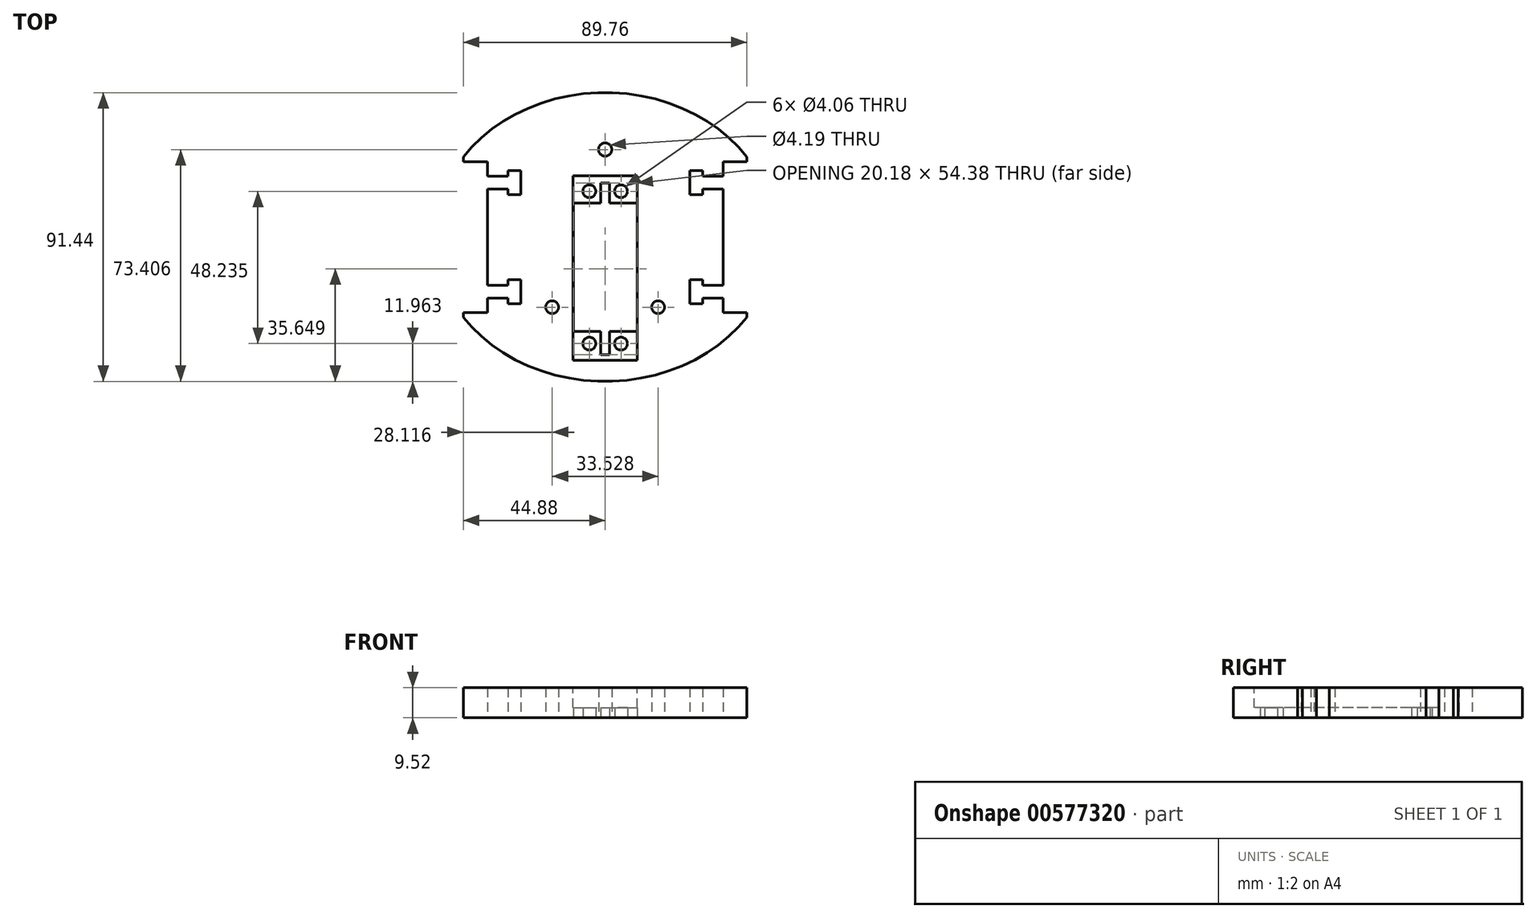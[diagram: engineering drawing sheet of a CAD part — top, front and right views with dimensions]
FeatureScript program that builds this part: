
annotation { "Feature Type Name" : "Feature", "Feature Type Description" : "" }
export const myFeature = defineFeature(function(context is Context, id is Id, definition is map)
    precondition{}
    {
        {
            var Q0;
            Q0=qCreatedBy(makeId("Top.planeOp"),FACE);
            var sketch = newSketch(context, id + "F0", { "sketchPlane" : qUnion([Q0])});
            skEllipticalArc(sketch, "E0", {});
            skLineSegment(sketch, "E1", {"start": v(44.88, 25.4) * mm, "end": v(44.88, 23.81) * mm});
            skLineSegment(sketch, "E2", {"start": v(0, 45.72) * mm, "end": v(0, 29.78) * mm});
            skArc(sketch, "E3", {"start": v(0, 25.6) * mm, "mid": v(2.1, 27.69) * mm, "end": v(0, 29.78) * mm});
            skCircle(sketch, "E4", {"center": v(5, 14.48) * mm, "radius": 2.03 * mm});
            skCircle(sketch, "E5", {"center": v(5, -33.76) * mm, "radius": 2.03 * mm});
            skLineSegment(sketch, "E6", {"start": v(44.88, 23.81) * mm, "end": v(37.26, 23.81) * mm});
            skLineSegment(sketch, "E7", {"start": v(37.26, 23.81) * mm, "end": v(37.26, 19.3) * mm});
            skLineSegment(sketch, "E8", {"start": v(37.26, 19.3) * mm, "end": v(30.78, 19.3) * mm});
            skLineSegment(sketch, "E9", {"start": v(30.78, 19.3) * mm, "end": v(30.78, 21.07) * mm});
            skLineSegment(sketch, "E10", {"start": v(30.78, 21.07) * mm, "end": v(26.72, 21.07) * mm});
            skLineSegment(sketch, "E11", {"start": v(26.72, 21.07) * mm, "end": v(26.72, 13.45) * mm});
            skLineSegment(sketch, "E12", {"start": v(26.72, 13.45) * mm, "end": v(30.78, 13.45) * mm});
            skLineSegment(sketch, "E13", {"start": v(30.78, 13.45) * mm, "end": v(30.78, 15.23) * mm});
            skLineSegment(sketch, "E14", {"start": v(30.78, 15.23) * mm, "end": v(37.26, 15.23) * mm});
            skLineSegment(sketch, "E15", {"start": v(37.26, 15.23) * mm, "end": v(37.26, -15.35) * mm});
            skLineSegment(sketch, "E16", {"start": v(37.26, -15.35) * mm, "end": v(30.78, -15.35) * mm});
            skLineSegment(sketch, "E17", {"start": v(30.78, -15.35) * mm, "end": v(30.78, -13.58) * mm});
            skLineSegment(sketch, "E18", {"start": v(30.78, -13.58) * mm, "end": v(26.72, -13.58) * mm});
            skLineSegment(sketch, "E19", {"start": v(26.72, -13.58) * mm, "end": v(26.72, -21.2) * mm});
            skLineSegment(sketch, "E20", {"start": v(26.72, -21.2) * mm, "end": v(30.78, -21.2) * mm});
            skLineSegment(sketch, "E21", {"start": v(30.78, -21.2) * mm, "end": v(30.78, -19.42) * mm});
            skLineSegment(sketch, "E22", {"start": v(30.78, -19.42) * mm, "end": v(37.26, -19.42) * mm});
            skLineSegment(sketch, "E23", {"start": v(37.26, -19.42) * mm, "end": v(37.26, -23.94) * mm});
            skLineSegment(sketch, "E24", {"start": v(37.26, -23.94) * mm, "end": v(44.88, -23.94) * mm});
            skLineSegment(sketch, "E25", {"start": v(0, 17.12) * mm, "end": v(1.36, 17.12) * mm});
            skLineSegment(sketch, "E26", {"start": v(1.36, 17.12) * mm, "end": v(1.36, 10.68) * mm});
            skLineSegment(sketch, "E27", {"start": v(1.36, 10.68) * mm, "end": v(10.1, 10.68) * mm});
            skLineSegment(sketch, "E28", {"start": v(10.1, 10.68) * mm, "end": v(10.1, -29.96) * mm});
            skLineSegment(sketch, "E29", {"start": v(10.1, -29.96) * mm, "end": v(1.36, -29.96) * mm});
            skLineSegment(sketch, "E30", {"start": v(1.36, -29.96) * mm, "end": v(1.36, -37.26) * mm});
            skLineSegment(sketch, "E31", {"start": v(1.36, -37.26) * mm, "end": v(0, -37.26) * mm});
            skLineSegment(sketch, "E32.trimOffspring", {"start": v(44.88, -23.94) * mm, "end": v(44.88, -25.4) * mm});
            skEllipticalArc(sketch, "E33.trimOffspring", {});
            skLineSegment(sketch, "E34.trimOffspring", {"start": v(0, -37.26) * mm, "end": v(0, -45.72) * mm});
            skLineSegment(sketch, "E35.trimOffspring", {"start": v(0, 25.6) * mm, "end": v(0, 17.12) * mm});
            skCircle(sketch, "E36", {"center": v(16.76, -22.23) * mm, "radius": 2.03 * mm});
            const initialGuessF0  = {"E0": [0, 0, -1, 0, 0.053975, 0.04572, 1.5707963267948966, 2.5525616833735194], "E33.trimOffspring": [0, 0, -1, 0, 0.053975, 0.04572, 3.7306236238060655, 4.71238898038469]};
            skSetInitialGuess(sketch, initialGuessF0);
            skSolve(sketch);
        }
        {
            var Q0;
            Q0 = qSketchRegion(id + "F0", true);
            extrude(context, id + "F1", {"entities" : qUnion([Q0]), "endBound" : BoundingType.SYMMETRIC, "depth" : 9.52 * mm, "offsetDistance" : 25.4 * mm});
        }
        {
            var Q0;
            Q0=makeQuery(id+"F1.opExtrude","CAP_FACE",FACE,{"disambiguationData":[OSD([sQuery(id+"F0.wireOp",EDGE,"E0"),sQuery(id+"F0.wireOp",EDGE,"E1"),sQuery(id+"F0.wireOp",EDGE,"E2"),sQuery(id+"F0.wireOp",EDGE,"E3"),sQuery(id+"F0.wireOp",EDGE,"E4"),sQuery(id+"F0.wireOp",EDGE,"E5"),sQuery(id+"F0.wireOp",EDGE,"E6"),sQuery(id+"F0.wireOp",EDGE,"E7"),sQuery(id+"F0.wireOp",EDGE,"E8"),sQuery(id+"F0.wireOp",EDGE,"E9"),sQuery(id+"F0.wireOp",EDGE,"E10"),sQuery(id+"F0.wireOp",EDGE,"E11"),sQuery(id+"F0.wireOp",EDGE,"E12"),sQuery(id+"F0.wireOp",EDGE,"E13"),sQuery(id+"F0.wireOp",EDGE,"E14"),sQuery(id+"F0.wireOp",EDGE,"E15"),sQuery(id+"F0.wireOp",EDGE,"E16"),sQuery(id+"F0.wireOp",EDGE,"E17"),sQuery(id+"F0.wireOp",EDGE,"E18"),sQuery(id+"F0.wireOp",EDGE,"E19"),sQuery(id+"F0.wireOp",EDGE,"E20"),sQuery(id+"F0.wireOp",EDGE,"E21"),sQuery(id+"F0.wireOp",EDGE,"E22"),sQuery(id+"F0.wireOp",EDGE,"E23"),sQuery(id+"F0.wireOp",EDGE,"E24"),sQuery(id+"F0.wireOp",EDGE,"E25"),sQuery(id+"F0.wireOp",EDGE,"E26"),sQuery(id+"F0.wireOp",EDGE,"E27"),sQuery(id+"F0.wireOp",EDGE,"E28"),sQuery(id+"F0.wireOp",EDGE,"E29"),sQuery(id+"F0.wireOp",EDGE,"E30"),sQuery(id+"F0.wireOp",EDGE,"E31"),sQuery(id+"F0.wireOp",EDGE,"E32.trimOffspring"),sQuery(id+"F0.wireOp",EDGE,"E33.trimOffspring"),sQuery(id+"F0.wireOp",EDGE,"E34.trimOffspring"),sQuery(id+"F0.wireOp",EDGE,"E35.trimOffspring")])],"isStart":false});
            var sketch = newSketch(context, id + "F2", { "sketchPlane" : qUnion([Q0])});
            skLineSegment(sketch, "E37.bottom", {"start": v(0, 19.34) * mm, "end": v(10.16, 19.34) * mm});
            skLineSegment(sketch, "E37.top", {"start": v(0, -39.08) * mm, "end": v(10.16, -39.08) * mm});
            skLineSegment(sketch, "E37.left", {"start": v(0, 19.34) * mm, "end": v(0, -39.08) * mm});
            skLineSegment(sketch, "E37.right", {"start": v(10.16, 19.34) * mm, "end": v(10.16, -39.08) * mm});
            skSolve(sketch);
        }
        {
            var Q0;
            Q0 = qSketchRegion(id + "F2", true);
            extrude(context, id + "F3", {"entities" : qUnion([Q0]), "operationType" : NewBodyOperationType.REMOVE, "oppositeDirection" : true, "depth" : 6.35 * mm, "offsetDistance" : 25.4 * mm});
        }
        {
            var Q0;
            Q0=makeQuery(id+"F1.opExtrude","SWEPT_BODY",BODY,{"disambiguationData":[OSD([sQuery(id+"F0.wireOp",EDGE,"E0"),sQuery(id+"F0.wireOp",EDGE,"E1"),sQuery(id+"F0.wireOp",EDGE,"E2"),sQuery(id+"F0.wireOp",EDGE,"E3"),sQuery(id+"F0.wireOp",EDGE,"E4"),sQuery(id+"F0.wireOp",EDGE,"E5"),sQuery(id+"F0.wireOp",EDGE,"E6"),sQuery(id+"F0.wireOp",EDGE,"E7"),sQuery(id+"F0.wireOp",EDGE,"E8"),sQuery(id+"F0.wireOp",EDGE,"E9"),sQuery(id+"F0.wireOp",EDGE,"E10"),sQuery(id+"F0.wireOp",EDGE,"E11"),sQuery(id+"F0.wireOp",EDGE,"E12"),sQuery(id+"F0.wireOp",EDGE,"E13"),sQuery(id+"F0.wireOp",EDGE,"E14"),sQuery(id+"F0.wireOp",EDGE,"E15"),sQuery(id+"F0.wireOp",EDGE,"E16"),sQuery(id+"F0.wireOp",EDGE,"E17"),sQuery(id+"F0.wireOp",EDGE,"E18"),sQuery(id+"F0.wireOp",EDGE,"E19"),sQuery(id+"F0.wireOp",EDGE,"E20"),sQuery(id+"F0.wireOp",EDGE,"E21"),sQuery(id+"F0.wireOp",EDGE,"E22"),sQuery(id+"F0.wireOp",EDGE,"E23"),sQuery(id+"F0.wireOp",EDGE,"E24"),sQuery(id+"F0.wireOp",EDGE,"E25"),sQuery(id+"F0.wireOp",EDGE,"E26"),sQuery(id+"F0.wireOp",EDGE,"E27"),sQuery(id+"F0.wireOp",EDGE,"E28"),sQuery(id+"F0.wireOp",EDGE,"E29"),sQuery(id+"F0.wireOp",EDGE,"E30"),sQuery(id+"F0.wireOp",EDGE,"E31"),sQuery(id+"F0.wireOp",EDGE,"E32.trimOffspring"),sQuery(id+"F0.wireOp",EDGE,"E33.trimOffspring"),sQuery(id+"F0.wireOp",EDGE,"E34.trimOffspring"),sQuery(id+"F0.wireOp",EDGE,"E35.trimOffspring")])]});
            var Q1;
            Q1=qCreatedBy(makeId("Right.planeOp"),FACE);
            mirror(context, id + "F4", {"operationType" : NewBodyOperationType.ADD, "entities" : qUnion([Q0]), "mirrorPlane" : qUnion([Q1])});
        }
    });
